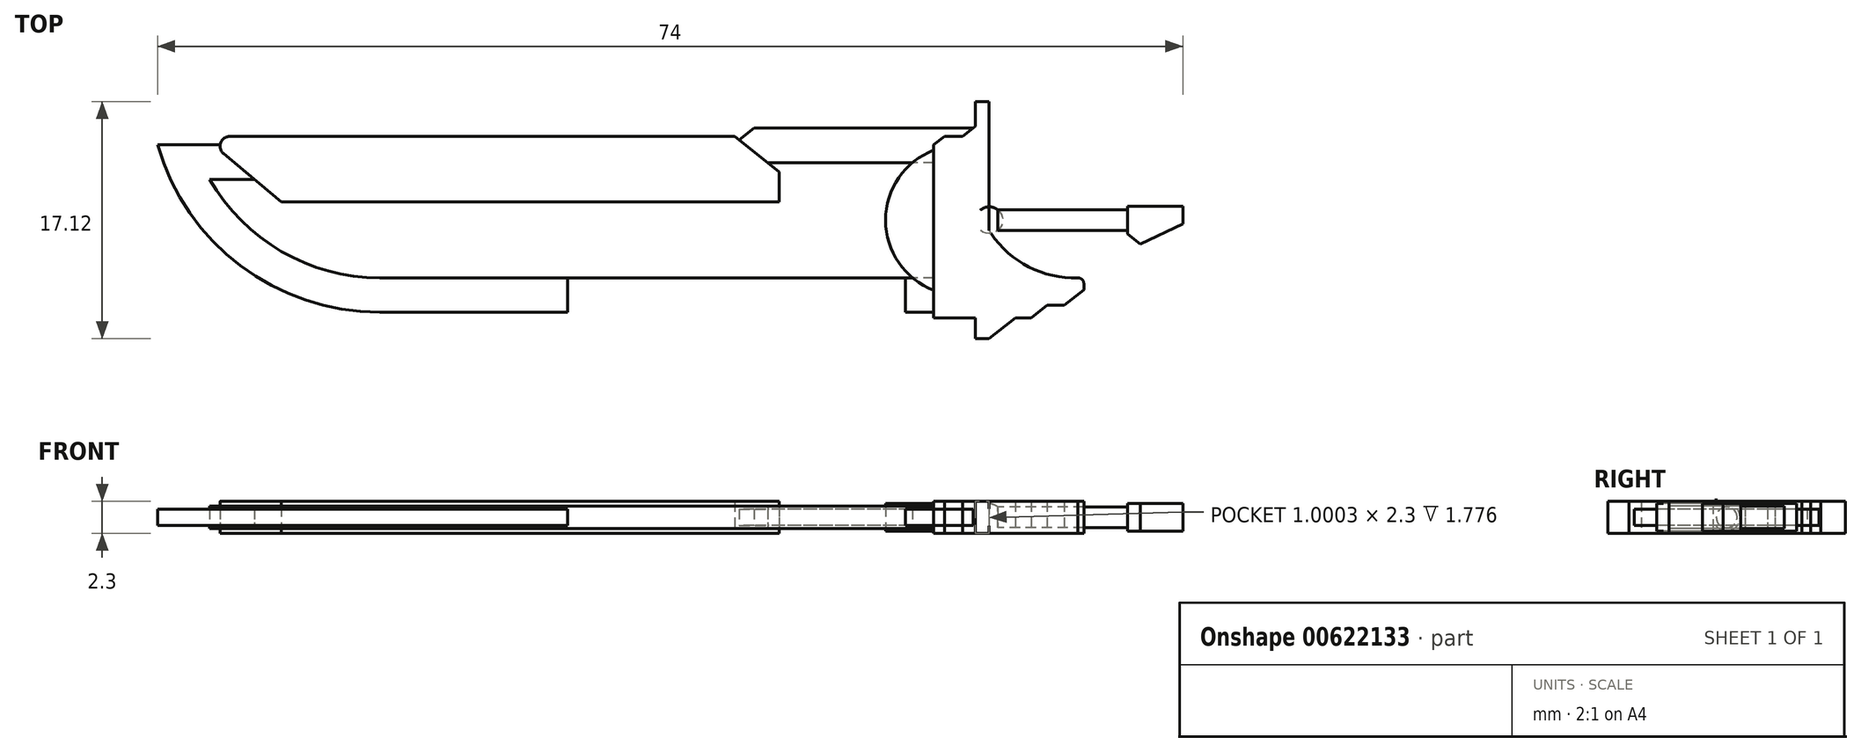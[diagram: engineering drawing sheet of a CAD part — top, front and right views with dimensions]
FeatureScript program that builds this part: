
annotation { "Feature Type Name" : "Feature", "Feature Type Description" : "" }
export const myFeature = defineFeature(function(context is Context, id is Id, definition is map)
    precondition{}
    {
        {
            var Q0;
            Q0=qCreatedBy(makeId("Top.planeOp"),FACE);
            var sketch = newSketch(context, id + "F0", { "sketchPlane" : qUnion([Q0])});
            skLineSegment(sketch, "E0", {"start": v(-17.33, -2.03) * mm, "end": v(-17.33, -14.53) * mm});
            skLineSegment(sketch, "E1", {"start": v(-17.33, -14.53) * mm, "end": v(-13.33, -14.53) * mm});
            skLineSegment(sketch, "E2", {"start": v(-13.33, -14.53) * mm, "end": v(-13.33, -0.41) * mm});
            skLineSegment(sketch, "E3", {"start": v(-13.33, -0.41) * mm, "end": v(-13.99, -0.41) * mm});
            skPoint(sketch, "E4.start.orphan", {"position": v(-13.33, -7.47) * mm});
            skLineSegment(sketch, "E5", {"start": v(-13.33, -14.53) * mm, "end": v(-10.3, -14.53) * mm});
            skLineSegment(sketch, "E6", {"start": v(-10.3, -14.53) * mm, "end": v(-9.15, -13.62) * mm});
            skLineSegment(sketch, "E7", {"start": v(-9.15, -13.62) * mm, "end": v(-7.9, -13.62) * mm});
            skLineSegment(sketch, "E8", {"start": v(-7.9, -13.62) * mm, "end": v(-6.5, -12.5) * mm});
            skLineSegment(sketch, "E9", {"start": v(-6.5, -12.5) * mm, "end": v(-6.5, -12.04) * mm});
            skPoint(sketch, "E10.visualSharp", {"position": v(-6.5, -11.6) * mm});
            skArc(sketch, "E10.filletArc", {"start": v(-6.5, -12.04) * mm, "mid": v(-6.63, -11.75) * mm, "end": v(-6.93, -11.64) * mm});
            skCircle(sketch, "E11", {"center": v(-53, 58.34) * mm, "radius": 11.76 * mm});
            skLineSegment(sketch, "E12", {"start": v(-53, 70.1) * mm, "end": v(-53, 46.59) * mm});
            skLineSegment(sketch, "E13", {"start": v(-17.33, -2.03) * mm, "end": v(-16.55, -1.4) * mm});
            skLineSegment(sketch, "E14", {"start": v(-16.55, -1.4) * mm, "end": v(-15.24, -1.4) * mm});
            skLineSegment(sketch, "E15", {"start": v(-15.24, -1.4) * mm, "end": v(-13.99, -0.41) * mm});
            skLineSegment(sketch, "E16", {"start": v(-3.36, 1.88) * mm, "end": v(-73.36, 1.88) * mm});
            skLineSegment(sketch, "E17", {"start": v(-17.33, -14.13) * mm, "end": v(-43.77, -14.13) * mm});
            skLineSegment(sketch, "E18.MirrorCS", {"start": v(-17.33, -2.03) * mm, "end": v(-18.12, -1.4) * mm});
            skLineSegment(sketch, "E19", {"start": v(-14.5, -0.81) * mm, "end": v(-30.3, -0.81) * mm});
            skLineSegment(sketch, "E20", {"start": v(-30.3, -0.81) * mm, "end": v(-31.83, -2.03) * mm});
            skLineSegment(sketch, "E21", {"start": v(-31.83, -2.03) * mm, "end": v(-57.33, -2.03) * mm});
            skLineSegment(sketch, "E22", {"start": v(-13.33, -7.47) * mm, "end": v(-17.33, -7.47) * mm});
            skLineSegment(sketch, "E23", {"start": v(-43.77, -2.03) * mm, "end": v(-43.77, -14.13) * mm});
            skLineSegment(sketch, "E24", {"start": v(-43.77, -8.08) * mm, "end": v(-46.21, -8.08) * mm});
            skPoint(sketch, "E24.endSnap0", {"position": v(-43.77, -8.08) * mm});
            skLineSegment(sketch, "E25.MirrorCS", {"start": v(-31.83, -14.13) * mm, "end": v(-43.77, -14.13) * mm});
            skLineSegment(sketch, "E26", {"start": v(-43.77, -14.13) * mm, "end": v(-57.33, -14.13) * mm});
            skLineSegment(sketch, "E27", {"start": v(-57.33, -2.03) * mm, "end": v(-73.36, -2.03) * mm});
            skArc(sketch, "E28", {"start": v(-73.36, -2.03) * mm, "mid": v(-67.37, -10.76) * mm, "end": v(-57.33, -14.13) * mm});
            skLineSegment(sketch, "E29", {"start": v(-64.14, -6.13) * mm, "end": v(-55.48, -6.13) * mm});
            skLineSegment(sketch, "E30", {"start": v(-55.48, -6.13) * mm, "end": v(-50.32, -2.03) * mm});
            skLineSegment(sketch, "E31", {"start": v(-55.48, -6.13) * mm, "end": v(-37, -6.13) * mm});
            skLineSegment(sketch, "E32", {"start": v(-19.37, -0.81) * mm, "end": v(-19.37, -14.13) * mm});
            skLineSegment(sketch, "E33", {"start": v(-18.69, -0.81) * mm, "end": v(-18.69, -2.41) * mm});
            skLineSegment(sketch, "E34", {"start": v(-18.56, -14.13) * mm, "end": v(-18.56, -12.53) * mm});
            skPoint(sketch, "E35", {"position": v(-17.33, -12.53) * mm});
            skPoint(sketch, "E36", {"position": v(-17.33, -2.41) * mm});
            skArc(sketch, "E37", {"start": v(-17.33, -2.41) * mm, "mid": v(-20.81, -7.47) * mm, "end": v(-17.33, -12.53) * mm});
            skLineSegment(sketch, "E38", {"start": v(-13.33, -7.47) * mm, "end": v(-11.3, -7.47) * mm});
            skLineSegment(sketch, "E39", {"start": v(-3.36, -6.72) * mm, "end": v(-11.43, -6.72) * mm});
            skLineSegment(sketch, "E40.MirrorCS", {"start": v(-3.36, -8.22) * mm, "end": v(-11.43, -8.22) * mm});
            skLineSegment(sketch, "E41", {"start": v(0.64, -6.72) * mm, "end": v(0.64, -7.72) * mm});
            skLineSegment(sketch, "E42", {"start": v(0.64, -7.72) * mm, "end": v(-2.23, -9.11) * mm});
            skLineSegment(sketch, "E43", {"start": v(-6.5, -12.5) * mm, "end": v(-6.5, -14.5) * mm});
            skLineSegment(sketch, "E44.MirrorCS", {"start": v(-5.1, -13.62) * mm, "end": v(-6.5, -12.5) * mm});
            skLineSegment(sketch, "E45", {"start": v(0.64, 1.88) * mm, "end": v(-3.36, 1.88) * mm});
            skLineSegment(sketch, "E46", {"start": v(0.64, 3.29) * mm, "end": v(-73.36, 3.29) * mm});
            skLineSegment(sketch, "E47", {"start": v(-34.55, -3.98) * mm, "end": v(-37, -2.03) * mm});
            skLineSegment(sketch, "E48", {"start": v(-34.55, -6.13) * mm, "end": v(-37, -6.13) * mm});
            skLineSegment(sketch, "E49", {"start": v(-50.32, -2.03) * mm, "end": v(-49.86, -1.67) * mm});
            skLineSegment(sketch, "E50", {"start": v(-49.86, -1.67) * mm, "end": v(-67.91, -1.67) * mm});
            skLineSegment(sketch, "E51", {"start": v(-37, -2.03) * mm, "end": v(-37.45, -1.67) * mm});
            skLineSegment(sketch, "E52", {"start": v(-37.45, -1.67) * mm, "end": v(-49.86, -1.67) * mm});
            skLineSegment(sketch, "E53", {"start": v(-34.55, -6.13) * mm, "end": v(-34.55, -3.98) * mm});
            skPoint(sketch, "E54.visualSharp", {"position": v(-69.02, -1.67) * mm});
            skPoint(sketch, "E55.end.orphan", {"position": v(-68.43, -2.72) * mm});
            skLineSegment(sketch, "E56", {"start": v(-37.45, -1.67) * mm, "end": v(-31.38, -1.67) * mm});
            skLineSegment(sketch, "E57", {"start": v(-31.38, -1.67) * mm, "end": v(-28.47, -3.98) * mm});
            skLineSegment(sketch, "E58", {"start": v(-28.47, -3.98) * mm, "end": v(-28.47, -6.13) * mm});
            skLineSegment(sketch, "E59", {"start": v(-28.47, -6.13) * mm, "end": v(-34.96, -6.13) * mm});
            skLineSegment(sketch, "E60", {"start": v(-31.38, -1.67) * mm, "end": v(-31.7, -1.42) * mm});
            skLineSegment(sketch, "E61", {"start": v(-31.7, -1.42) * mm, "end": v(-68.15, -1.42) * mm});
            skPoint(sketch, "E62.visualSharp", {"position": v(-70.08, -1.42) * mm});
            skArc(sketch, "E62.filletArc", {"start": v(-68.15, -1.42) * mm, "mid": v(-68.8, -1.88) * mm, "end": v(-68.6, -2.66) * mm});
            skLineSegment(sketch, "E63", {"start": v(-68.6, -2.66) * mm, "end": v(-64.44, -6.13) * mm});
            skLineSegment(sketch, "E64", {"start": v(-64.44, -6.13) * mm, "end": v(-64.14, -6.13) * mm});
            skLineSegment(sketch, "E65", {"start": v(-11.43, -6.72) * mm, "end": v(-13.33, -6.72) * mm});
            skLineSegment(sketch, "E66", {"start": v(-11.43, -8.22) * mm, "end": v(-13.33, -8.22) * mm});
            skCircle(sketch, "E67.0", {"center": v(-13.33, -7.47) * mm, "radius": 0.97 * mm});
            skLineSegment(sketch, "E68", {"start": v(-11.3, -7.47) * mm, "end": v(-5.92, -7.47) * mm});
            skPoint(sketch, "E69.MirrorCS.end.orphan", {"position": v(-3.36, -8.22) * mm});
            skLineSegment(sketch, "E70", {"start": v(-3.36, -8.22) * mm, "end": v(-3.36, -6.72) * mm});
            skLineSegment(sketch, "E71", {"start": v(-5.92, -7.47) * mm, "end": v(-3.36, -7.47) * mm});
            skArc(sketch, "E72", {"start": v(-13.33, -8.22) * mm, "mid": v(-10.59, -10.78) * mm, "end": v(-6.93, -11.64) * mm});
            skArc(sketch, "E73.trimOffspring", {"start": v(-11.43, -6.72) * mm, "mid": v(-11.3, -7.47) * mm, "end": v(-11.43, -8.22) * mm});
            skPoint(sketch, "E74.start.orphan", {"position": v(-15.38, -7.47) * mm});
            skLineSegment(sketch, "E75", {"start": v(-3.36, -7.47) * mm, "end": v(-3.36, -6.72) * mm});
            skLineSegment(sketch, "E76", {"start": v(-3.36, -7.47) * mm, "end": v(-3.36, -6.47) * mm});
            skLineSegment(sketch, "E77", {"start": v(-3.36, -7.47) * mm, "end": v(-3.36, -8.47) * mm});
            skLineSegment(sketch, "E78", {"start": v(-3.36, -8.47) * mm, "end": v(-2.43, -9.2) * mm});
            skLineSegment(sketch, "E79", {"start": v(-2.23, -9.11) * mm, "end": v(-2.43, -9.2) * mm});
            skLineSegment(sketch, "E80", {"start": v(-3.36, -6.47) * mm, "end": v(0.64, -6.47) * mm});
            skLineSegment(sketch, "E81", {"start": v(0.64, -6.47) * mm, "end": v(0.64, -6.72) * mm});
            skPoint(sketch, "E82.orphan", {"position": v(-2.23, -9.36) * mm});
            skLineSegment(sketch, "E83.0", {"start": v(-31.83, -11.63) * mm, "end": v(-43.77, -11.63) * mm});
            skLineSegment(sketch, "E83.1", {"start": v(-43.77, -11.63) * mm, "end": v(-57.33, -11.63) * mm});
            skArc(sketch, "E83.2", {"start": v(-69.6, -4.53) * mm, "mid": v(-64.42, -9.72) * mm, "end": v(-57.33, -11.63) * mm});
            skLineSegment(sketch, "E83.3", {"start": v(-57.33, -4.53) * mm, "end": v(-69.6, -4.53) * mm});
            skLineSegment(sketch, "E84.0", {"start": v(-29.43, -3.31) * mm, "end": v(-30.28, -3.98) * mm});
            skLineSegment(sketch, "E84.1", {"start": v(-14.5, -3.31) * mm, "end": v(-29.43, -3.31) * mm});
            skLineSegment(sketch, "E85", {"start": v(-31.83, -11.63) * mm, "end": v(-17.33, -11.63) * mm});
            skLineSegment(sketch, "E86", {"start": v(-57.33, -4.53) * mm, "end": v(-30.28, -3.98) * mm});
            skPoint(sketch, "E87.orphan", {"position": v(-13.33, 0) * mm});
            skLineSegment(sketch, "E88", {"start": v(-14.34, 0.69) * mm, "end": v(-14.34, -0.69) * mm});
            skLineSegment(sketch, "E89", {"start": v(-13.33, -0.41) * mm, "end": v(-13.33, 0.69) * mm});
            skPoint(sketch, "E90.end.orphan", {"position": v(-13.99, 0.69) * mm});
            skLineSegment(sketch, "E91", {"start": v(-13.33, 0.69) * mm, "end": v(-13.33, 1.09) * mm});
            skLineSegment(sketch, "E92", {"start": v(-13.33, 1.09) * mm, "end": v(-14.34, 1.09) * mm});
            skLineSegment(sketch, "E93", {"start": v(-14.34, 1.09) * mm, "end": v(-14.34, 0.69) * mm});
            skLineSegment(sketch, "E94.MirrorCS", {"start": v(-13.33, -16.03) * mm, "end": v(-14.34, -16.03) * mm});
            skLineSegment(sketch, "E95.MirrorCS", {"start": v(-14.34, -15.63) * mm, "end": v(-14.34, -14.25) * mm});
            skLineSegment(sketch, "E96.MirrorCS", {"start": v(-14.34, -16.03) * mm, "end": v(-14.34, -15.63) * mm});
            skLineSegment(sketch, "E97", {"start": v(-13.33, -16.03) * mm, "end": v(-11.45, -14.53) * mm});
            skPoint(sketch, "E98.MirrorCS.end.orphan", {"position": v(-13.33, -15.63) * mm});
            skPoint(sketch, "E98.MirrorCS.start.orphan", {"position": v(-13.33, -14.53) * mm});
            skPoint(sketch, "E99.MirrorCS.end.orphan", {"position": v(-13.33, -16.03) * mm});
            skLineSegment(sketch, "E100", {"start": v(5.63, 1.09) * mm, "end": v(5.63, -16.03) * mm});
            skLineSegment(sketch, "E101", {"start": v(-14.34, 4.18) * mm, "end": v(-73.36, 4.18) * mm});
            skLineSegment(sketch, "E102", {"start": v(-13.33, -0.41) * mm, "end": v(-13.33, -14.53) * mm});
            skSolve(sketch);
        }
        {
            var Q0;
            {var subQ0=sQuery(id+"F0.wireOp",EDGE,"E65");var subQ1=sQuery(id+"F0.wireOp",EDGE,"E2");var subQ2=makeQuery(id+"F0.imprint","INTERSECT",VERTEX,{"derivedFrom":[subQ1,subQ0]});Q0=makeQuery(id+"F0.imprint","IMPRINT",FACE,{"disambiguationData":[TD([[makeQuery(id+"F0.imprint","IMPRINT",EDGE,{"disambiguationData":[TD([[subQ2,-1.0]])],"derivedFrom":subQ1}),-1.0]])]});}
            var Q1;
            {var subQ1=sQuery(id+"F0.wireOp",EDGE,"E2");var subQ3=sQuery(id+"F0.wireOp",EDGE,"E65");var subQ4=makeQuery(id+"F0.imprint","INTERSECT",VERTEX,{"derivedFrom":[subQ1,subQ3]});Q1=makeQuery(id+"F0.imprint","IMPRINT",FACE,{"disambiguationData":[TD([[makeQuery(id+"F0.imprint","IMPRINT",EDGE,{"disambiguationData":[TD([[subQ4,1.0]])],"derivedFrom":subQ3}),1.0]])]});}
            var Q2;
            Q2=sQuery(id+"F0.wireOp",EDGE,"E38");
            revolve(context, id + "F1", {"entities" : qUnion([Q0, Q1]), "axis" : qUnion([Q2]), "revolveType" : RevolveType.FULL});
        }
        {
            var Q0;
            {var subQ0=sQuery(id+"F0.wireOp",EDGE,"E38");var subQ5=sQuery(id+"F0.wireOp",EDGE,"E67.0");var subQ6=makeQuery(id+"F0.imprint","INTERSECT",VERTEX,{"derivedFrom":[subQ0,subQ5]});Q0=makeQuery(id+"F0.imprint","IMPRINT",FACE,{"disambiguationData":[TD([[makeQuery(id+"F0.imprint","IMPRINT",EDGE,{"disambiguationData":[TD([[subQ6,-1.0]])],"derivedFrom":subQ5}),-1.0]])]});}
            var Q1;
            {var subQ1=sQuery(id+"F0.wireOp",EDGE,"E39");Q1=makeQuery(id+"F0.imprint","IMPRINT",FACE,{"disambiguationData":[TD([[makeQuery(id+"F0.imprint","IMPRINT",EDGE,{"derivedFrom":subQ1}),1.0]])]});}
            var Q2;
            {var subQ0=sQuery(id+"F0.wireOp",EDGE,"E102");var subQ1=sQuery(id+"F0.wireOp",EDGE,"E65");var subQ2=makeQuery(id+"F0.imprint","INTERSECT",VERTEX,{"derivedFrom":[subQ1,subQ0]});Q2=makeQuery(id+"F0.imprint","IMPRINT",FACE,{"disambiguationData":[TD([[makeQuery(id+"F0.imprint","IMPRINT",EDGE,{"disambiguationData":[TD([[subQ2,1.0]])],"derivedFrom":subQ1}),-1.0]])]});}
            var Q3;
            Q3=sQuery(id+"F0.wireOp",EDGE,"E38");
            revolve(context, id + "F2", {"operationType" : NewBodyOperationType.ADD, "entities" : qUnion([Q0, Q1, Q2]), "axis" : qUnion([Q3]), "revolveType" : RevolveType.FULL});
        }
        {
            var Q0;
            {var subQ0=sQuery(id+"F0.wireOp",EDGE,"E3");Q0=makeQuery(id+"F0.imprint","IMPRINT",FACE,{"disambiguationData":[TD([[makeQuery(id+"F0.imprint","IMPRINT",EDGE,{"derivedFrom":subQ0}),1.0]])]});}
            var Q1;
            {var subQ0=sQuery(id+"F0.wireOp",EDGE,"E1");Q1=makeQuery(id+"F0.imprint","IMPRINT",FACE,{"disambiguationData":[TD([[makeQuery(id+"F0.imprint","IMPRINT",EDGE,{"derivedFrom":subQ0}),1.0]])]});}
            var Q2;
            {var subQ0=sQuery(id+"F0.wireOp",EDGE,"E5");Q2=makeQuery(id+"F0.imprint","IMPRINT",FACE,{"disambiguationData":[TD([[makeQuery(id+"F0.imprint","IMPRINT",EDGE,{"derivedFrom":subQ0}),1.0]])]});}
            var Q3;
            {var subQ0=sQuery(id+"F0.wireOp",EDGE,"E2");var subQ2=sQuery(id+"F0.wireOp",EDGE,"E67.0");var subQ3=makeQuery(id+"F0.imprint","INTERSECT",VERTEX,{"disambiguationData":[OD(1.0)],"derivedFrom":[subQ0,subQ2]});Q3=makeQuery(id+"F0.imprint","IMPRINT",FACE,{"disambiguationData":[TD([[makeQuery(id+"F0.imprint","IMPRINT",EDGE,{"disambiguationData":[TD([[subQ3,1.0]])],"derivedFrom":subQ2}),1.0]])]});}
            var Q4;
            {var subQ1=sQuery(id+"F0.wireOp",EDGE,"E2");var subQ3=makeQuery(id+"F0.imprint","INTERSECT",VERTEX,{"derivedFrom":[subQ1,sQuery(id+"F0.wireOp",EDGE,"E65")]});Q4=makeQuery(id+"F0.imprint","IMPRINT",FACE,{"disambiguationData":[TD([[makeQuery(id+"F0.imprint","IMPRINT",EDGE,{"disambiguationData":[TD([[subQ3,-1.0]])],"derivedFrom":subQ1}),1.0]])]});}
            var Q5;
            {var subQ0=sQuery(id+"F0.wireOp",EDGE,"E72");var subQ3=sQuery(id+"F0.wireOp",EDGE,"E67.0");var subQ5=makeQuery(id+"F0.imprint","INTERSECT",VERTEX,{"derivedFrom":[subQ3,subQ0]});Q5=makeQuery(id+"F0.imprint","IMPRINT",FACE,{"disambiguationData":[TD([[makeQuery(id+"F0.imprint","IMPRINT",EDGE,{"disambiguationData":[TD([[subQ5,1.0]])],"derivedFrom":subQ3}),1.0]])]});}
            var Q6;
            Q6=makeQuery(id+"F0.imprint","IMPRINT",FACE,{"disambiguationData":[TD([[makeQuery(id+"F0.imprint","IMPRINT",EDGE,{"derivedFrom":sQuery(id+"F0.wireOp",EDGE,"E94.MirrorCS")}),-1.0]])]});
            var Q7;
            {var subQ2=sQuery(id+"F0.wireOp",EDGE,"E3");Q7=makeQuery(id+"F0.imprint","IMPRINT",FACE,{"disambiguationData":[TD([[makeQuery(id+"F0.imprint","IMPRINT",EDGE,{"derivedFrom":subQ2}),-1.0]])]});}
            var Q8;
            {var subQ0=sQuery(id+"F0.wireOp",EDGE,"E102");var subQ3=sQuery(id+"F0.wireOp",EDGE,"E67.0");var subQ6=makeQuery(id+"F0.imprint","INTERSECT",VERTEX,{"disambiguationData":[OD(0.0)],"derivedFrom":[subQ3,subQ0]});Q8=makeQuery(id+"F0.imprint","IMPRINT",FACE,{"disambiguationData":[TD([[makeQuery(id+"F0.imprint","IMPRINT",EDGE,{"disambiguationData":[TD([[subQ6,-1.0]])],"derivedFrom":subQ3}),1.0]])]});}
            var Q9;
            {var subQ1=sQuery(id+"F0.wireOp",EDGE,"E22");var subQ3=sQuery(id+"F0.wireOp",EDGE,"E67.0");var subQ4=makeQuery(id+"F0.imprint","INTERSECT",VERTEX,{"derivedFrom":[subQ1,subQ3]});Q9=makeQuery(id+"F0.imprint","IMPRINT",FACE,{"disambiguationData":[TD([[makeQuery(id+"F0.imprint","IMPRINT",EDGE,{"disambiguationData":[TD([[subQ4,-1.0]])],"derivedFrom":subQ3}),1.0]])]});}
            extrude(context, id + "F3", {"entities" : qUnion([Q0, Q1, Q2, Q3, Q4, Q5, Q6, Q7, Q8, Q9]), "operationType" : NewBodyOperationType.ADD, "endBound" : BoundingType.SYMMETRIC, "depth" : 2.3 * mm, "offsetDistance" : 25 * mm});
        }
        {
            var Q0;
            Q0=makeQuery(id+"F0.imprint","IMPRINT",FACE,{"disambiguationData":[TD([[makeQuery(id+"F0.imprint","IMPRINT",EDGE,{"derivedFrom":sQuery(id+"F0.wireOp",EDGE,"E41")}),-1.0]])]});
            extrude(context, id + "F4", {"entities" : qUnion([Q0]), "operationType" : NewBodyOperationType.ADD, "endBound" : BoundingType.SYMMETRIC, "depth" : 2 * mm, "offsetDistance" : 25 * mm});
        }
        {
            var Q0;
            Q0=makeQuery(id+"F0.imprint","IMPRINT",FACE,{"disambiguationData":[TD([[makeQuery(id+"F0.imprint","IMPRINT",EDGE,{"derivedFrom":sQuery(id+"F0.wireOp",EDGE,"E29")}),1.0]])]});
            var Q1;
            {var subQ0=sQuery(id+"F0.wireOp",EDGE,"E49");Q1=makeQuery(id+"F0.imprint","IMPRINT",FACE,{"disambiguationData":[TD([[makeQuery(id+"F0.imprint","IMPRINT",EDGE,{"derivedFrom":subQ0}),1.0]])]});}
            var Q2;
            {var subQ3=sQuery(id+"F0.wireOp",EDGE,"E30");Q2=makeQuery(id+"F0.imprint","IMPRINT",FACE,{"disambiguationData":[TD([[makeQuery(id+"F0.imprint","IMPRINT",EDGE,{"derivedFrom":subQ3}),-1.0]])]});}
            var Q3;
            {var subQ0=sQuery(id+"F0.wireOp",EDGE,"E47");Q3=makeQuery(id+"F0.imprint","IMPRINT",FACE,{"disambiguationData":[TD([[makeQuery(id+"F0.imprint","IMPRINT",EDGE,{"derivedFrom":subQ0}),1.0]])]});}
            var Q4;
            {var subQ1=sQuery(id+"F0.wireOp",EDGE,"E49");Q4=makeQuery(id+"F0.imprint","IMPRINT",FACE,{"disambiguationData":[TD([[makeQuery(id+"F0.imprint","IMPRINT",EDGE,{"derivedFrom":subQ1}),-1.0]])]});}
            var Q5;
            {var subQ1=sQuery(id+"F0.wireOp",EDGE,"E47");Q5=makeQuery(id+"F0.imprint","IMPRINT",FACE,{"disambiguationData":[TD([[makeQuery(id+"F0.imprint","IMPRINT",EDGE,{"derivedFrom":subQ1}),-1.0]])]});}
            var Q6;
            {var subQ4=sQuery(id+"F0.wireOp",EDGE,"E51");Q6=makeQuery(id+"F0.imprint","IMPRINT",FACE,{"disambiguationData":[TD([[makeQuery(id+"F0.imprint","IMPRINT",EDGE,{"derivedFrom":subQ4}),-1.0]])]});}
            var Q7;
            {var subQ3=sQuery(id+"F0.wireOp",EDGE,"E27");var subQ6=sQuery(id+"F0.wireOp",EDGE,"E21");var subQ12=makeQuery(id+"F0.imprint","INTERSECT",VERTEX,{"derivedFrom":[subQ6,subQ3]});Q7=makeQuery(id+"F0.imprint","IMPRINT",FACE,{"disambiguationData":[TD([[makeQuery(id+"F0.imprint","IMPRINT",EDGE,{"disambiguationData":[TD([[subQ12,-1.0]])],"derivedFrom":subQ3}),1.0]])]});}
            var Q8;
            {var subQ0=sQuery(id+"F0.wireOp",EDGE,"E48");Q8=makeQuery(id+"F0.imprint","IMPRINT",FACE,{"disambiguationData":[TD([[makeQuery(id+"F0.imprint","IMPRINT",EDGE,{"derivedFrom":subQ0}),-1.0]])]});}
            var Q9;
            {var subQ3=sQuery(id+"F0.wireOp",EDGE,"E58");Q9=makeQuery(id+"F0.imprint","IMPRINT",FACE,{"disambiguationData":[TD([[makeQuery(id+"F0.imprint","IMPRINT",EDGE,{"derivedFrom":subQ3}),-1.0]])]});}
            extrude(context, id + "F5", {"entities" : qUnion([Q0, Q1, Q2, Q3, Q4, Q5, Q6, Q7, Q8, Q9]), "endBound" : BoundingType.SYMMETRIC, "depth" : 2.3 * mm, "offsetDistance" : 25 * mm});
        }
        {
            var Q0;
            {var subQ0=sQuery(id+"F0.wireOp",EDGE,"E26");Q0=makeQuery(id+"F0.imprint","IMPRINT",FACE,{"disambiguationData":[TD([[makeQuery(id+"F0.imprint","IMPRINT",EDGE,{"derivedFrom":subQ0}),-1.0]])]});}
            var Q1;
            {var subQ8=sQuery(id+"F0.wireOp",EDGE,"E25.MirrorCS");Q1=makeQuery(id+"F0.imprint","IMPRINT",FACE,{"disambiguationData":[TD([[makeQuery(id+"F0.imprint","IMPRINT",EDGE,{"derivedFrom":subQ8}),-1.0]])]});}
            var Q2;
            {var subQ4=sQuery(id+"F0.wireOp",EDGE,"E13");Q2=makeQuery(id+"F0.imprint","IMPRINT",FACE,{"disambiguationData":[TD([[makeQuery(id+"F0.imprint","IMPRINT",EDGE,{"derivedFrom":subQ4}),1.0]])]});}
            var Q3;
            {var subQ1=sQuery(id+"F0.wireOp",EDGE,"E17");var subQ5=makeQuery(id+"F0.imprint","IMPRINT",VERTEX,{"derivedFrom":subQ1});Q3=makeQuery(id+"F0.imprint","IMPRINT",FACE,{"disambiguationData":[TD([[makeQuery(id+"F0.imprint","IMPRINT",EDGE,{"disambiguationData":[TD([[subQ5,1.0]])],"derivedFrom":subQ1}),-1.0]])]});}
            var Q4;
            {var subQ1=sQuery(id+"F0.wireOp",EDGE,"E20");var subQ6=sQuery(id+"F0.wireOp",EDGE,"E19");var subQ9=makeQuery(id+"F0.imprint","INTERSECT",VERTEX,{"derivedFrom":[subQ6,subQ1]});Q4=makeQuery(id+"F0.imprint","IMPRINT",FACE,{"disambiguationData":[TD([[makeQuery(id+"F0.imprint","IMPRINT",EDGE,{"disambiguationData":[TD([[subQ9,1.0]])],"derivedFrom":subQ6}),1.0]])]});}
            extrude(context, id + "F6", {"entities" : qUnion([Q0, Q1, Q2, Q3, Q4]), "endBound" : BoundingType.SYMMETRIC, "depth" : 1.2 * mm, "offsetDistance" : 25 * mm});
        }
        {
            var Q0;
            {var subQ0=sQuery(id+"F0.wireOp",EDGE,"E29");Q0=makeQuery(id+"F0.imprint","IMPRINT",FACE,{"disambiguationData":[TD([[makeQuery(id+"F0.imprint","IMPRINT",EDGE,{"derivedFrom":subQ0}),-1.0]])]});}
            var Q1;
            {var subQ8=sQuery(id+"F0.wireOp",EDGE,"E48");Q1=makeQuery(id+"F0.imprint","IMPRINT",FACE,{"disambiguationData":[TD([[makeQuery(id+"F0.imprint","IMPRINT",EDGE,{"derivedFrom":subQ8}),1.0]])]});}
            var Q2;
            {var subQ0=sQuery(id+"F0.wireOp",EDGE,"E37");var subQ1=sQuery(id+"F0.wireOp",EDGE,"E32");var subQ2=makeQuery(id+"F0.imprint","INTERSECT",VERTEX,{"disambiguationData":[OD(1.0)],"derivedFrom":[subQ1,subQ0]});Q2=makeQuery(id+"F0.imprint","IMPRINT",FACE,{"disambiguationData":[TD([[makeQuery(id+"F0.imprint","IMPRINT",EDGE,{"disambiguationData":[TD([[subQ2,-1.0]])],"derivedFrom":subQ1}),1.0]])]});}
            var Q3;
            {var subQ0=sQuery(id+"F0.wireOp",EDGE,"E84.1");var subQ1=sQuery(id+"F0.wireOp",EDGE,"E32");var subQ2=makeQuery(id+"F0.imprint","INTERSECT",VERTEX,{"derivedFrom":[subQ1,subQ0]});Q3=makeQuery(id+"F0.imprint","IMPRINT",FACE,{"disambiguationData":[TD([[makeQuery(id+"F0.imprint","IMPRINT",EDGE,{"disambiguationData":[TD([[subQ2,-1.0]])],"derivedFrom":subQ1}),1.0]])]});}
            var Q4;
            {var subQ6=sQuery(id+"F0.wireOp",EDGE,"E0");var subQ7=makeQuery(id+"F0.imprint","INTERSECT",VERTEX,{"derivedFrom":[subQ6,sQuery(id+"F0.wireOp",EDGE,"E22")]});Q4=makeQuery(id+"F0.imprint","IMPRINT",FACE,{"disambiguationData":[TD([[makeQuery(id+"F0.imprint","IMPRINT",EDGE,{"disambiguationData":[TD([[subQ7,1.0]])],"derivedFrom":subQ6}),-1.0]])]});}
            var Q5;
            {var subQ0=sQuery(id+"F0.wireOp",EDGE,"E37");var subQ1=sQuery(id+"F0.wireOp",EDGE,"E32");var subQ2=makeQuery(id+"F0.imprint","INTERSECT",VERTEX,{"disambiguationData":[OD(0.0)],"derivedFrom":[subQ1,subQ0]});Q5=makeQuery(id+"F0.imprint","IMPRINT",FACE,{"disambiguationData":[TD([[makeQuery(id+"F0.imprint","IMPRINT",EDGE,{"disambiguationData":[TD([[subQ2,-1.0]])],"derivedFrom":subQ1}),-1.0]])]});}
            extrude(context, id + "F7", {"entities" : qUnion([Q0, Q1, Q2, Q3, Q4, Q5]), "endBound" : BoundingType.SYMMETRIC, "depth" : 1.6 * mm, "offsetDistance" : 25 * mm});
        }
        {
            var Q0;
            {var subQ6=sQuery(id+"F0.wireOp",EDGE,"E0");var subQ7=makeQuery(id+"F0.imprint","INTERSECT",VERTEX,{"derivedFrom":[subQ6,sQuery(id+"F0.wireOp",EDGE,"E22")]});Q0=makeQuery(id+"F0.imprint","IMPRINT",FACE,{"disambiguationData":[TD([[makeQuery(id+"F0.imprint","IMPRINT",EDGE,{"disambiguationData":[TD([[subQ7,1.0]])],"derivedFrom":subQ6}),-1.0]])]});}
            var Q1;
            {var subQ0=sQuery(id+"F0.wireOp",EDGE,"E37");var subQ1=sQuery(id+"F0.wireOp",EDGE,"E0");var subQ2=makeQuery(id+"F0.imprint","INTERSECT",VERTEX,{"disambiguationData":[OD(0.0)],"derivedFrom":[subQ1,subQ0]});Q1=makeQuery(id+"F0.imprint","IMPRINT",FACE,{"disambiguationData":[TD([[makeQuery(id+"F0.imprint","IMPRINT",EDGE,{"disambiguationData":[TD([[subQ2,-1.0]])],"derivedFrom":subQ1}),-1.0]])]});}
            var Q2;
            {var subQ0=sQuery(id+"F0.wireOp",EDGE,"E37");var subQ1=sQuery(id+"F0.wireOp",EDGE,"E32");var subQ2=makeQuery(id+"F0.imprint","INTERSECT",VERTEX,{"disambiguationData":[OD(0.0)],"derivedFrom":[subQ1,subQ0]});Q2=makeQuery(id+"F0.imprint","IMPRINT",FACE,{"disambiguationData":[TD([[makeQuery(id+"F0.imprint","IMPRINT",EDGE,{"disambiguationData":[TD([[subQ2,-1.0]])],"derivedFrom":subQ1}),-1.0]])]});}
            var Q3;
            {var subQ0=sQuery(id+"F0.wireOp",EDGE,"E37");var subQ1=sQuery(id+"F0.wireOp",EDGE,"E0");var subQ2=makeQuery(id+"F0.imprint","INTERSECT",VERTEX,{"disambiguationData":[OD(1.0)],"derivedFrom":[subQ1,subQ0]});Q3=makeQuery(id+"F0.imprint","IMPRINT",FACE,{"disambiguationData":[TD([[makeQuery(id+"F0.imprint","IMPRINT",EDGE,{"disambiguationData":[TD([[subQ2,1.0]])],"derivedFrom":subQ1}),-1.0]])]});}
            extrude(context, id + "F8", {"entities" : qUnion([Q0, Q1, Q2, Q3]), "endBound" : BoundingType.SYMMETRIC, "depth" : 2 * mm, "offsetDistance" : 25 * mm});
        }
    });
